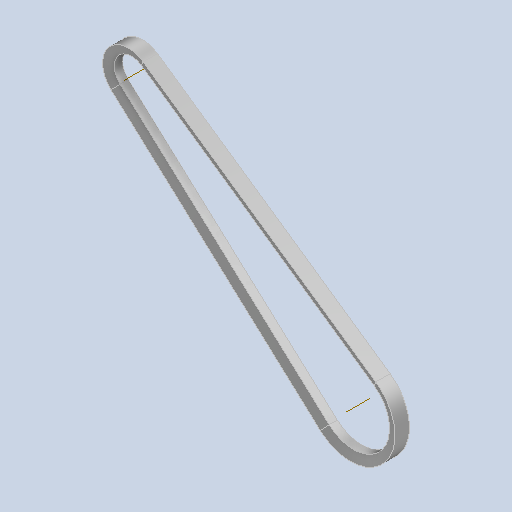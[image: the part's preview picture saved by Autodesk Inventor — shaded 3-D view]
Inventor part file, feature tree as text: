
AUTODESK INVENTOR PART (.ipt)
format: ipt  version: 2023 (Build 270158000, 158)  size: 109,568 bytes
history: native  units: mm (DEFAULTED — no unit token found)
features: other x5, sweep x1
ambient origin geometry x8: Origin, YZ Plane, XZ Plane, XY Plane, X Axis, Y Axis, Z Axis, Center Point
bodies: Solid1 (feature_tree)
feature tree (6):
  other  "Эскизная траектория"
  other  "Плоскость сечения"
  other  "РабОсь1"
  other  "РабОсь2"
  sweep  "Ремень"
  other  "Сечение"
